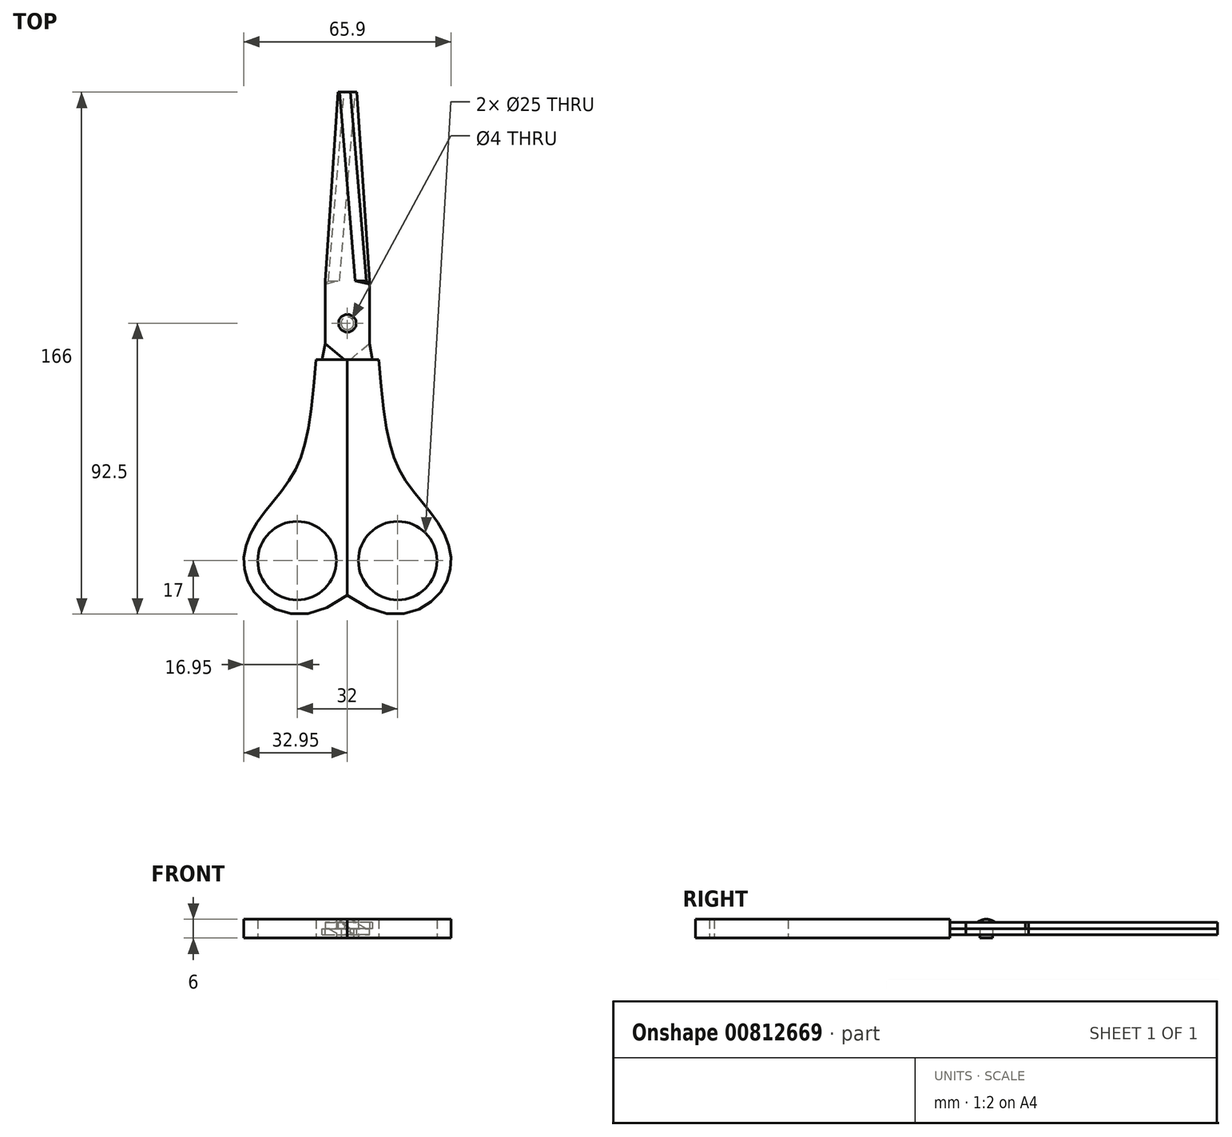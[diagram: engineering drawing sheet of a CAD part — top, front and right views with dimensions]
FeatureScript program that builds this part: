
annotation { "Feature Type Name" : "Feature", "Feature Type Description" : "" }
export const myFeature = defineFeature(function(context is Context, id is Id, definition is map)
    precondition{}
    {
        {
            var Q0;
            Q0=qCreatedBy(makeId("Top.planeOp"),FACE);
            var sketch = newSketch(context, id + "F0", { "sketchPlane" : qUnion([Q0])});
            skLineSegment(sketch, "E0", {"start": v(10, 0) * mm, "end": v(0, 0) * mm});
            skLineSegment(sketch, "E1", {"start": v(0, 0) * mm, "end": v(0, -75) * mm});
            skFitSpline(sketch, "E2", {"points": [v(10, 0) * mm, v(18.6, -38.65) * mm, v(31.21, -56.2) * mm, v(29.97, -73.56) * mm, v(0, -75) * mm], "startDerivative": vector(15.7, -213.23) * mm, "endDerivative": vector(-155.18, 117.57) * mm});
            skSolve(sketch);
        }
        {
            var Q0;
            Q0 = qSketchRegion(id + "F0", true);
            extrude(context, id + "F1", {"entities" : qUnion([Q0]), "depth" : 6 * mm, "offsetDistance" : 25 * mm});
        }
        {
            var Q0;
            Q0=qCreatedBy(makeId("Top.planeOp"),FACE);
            var sketch = newSketch(context, id + "F2", { "sketchPlane" : qUnion([Q0])});
            skCircle(sketch, "E3", {"center": v(16, -64) * mm, "radius": 12.5 * mm});
            skSolve(sketch);
        }
        {
            var Q0;
            Q0 = qSketchRegion(id + "F2", true);
            extrude(context, id + "F3", {"entities" : qUnion([Q0]), "depth" : 6 * mm, "offsetDistance" : 25 * mm});
        }
        {
            var Q0;
            Q0=makeQuery(id+"F3.opExtrude","SWEPT_BODY",BODY,{"disambiguationData":[OSD([sQuery(id+"F2.wireOp",EDGE,"E3")])]});
            var Q1;
            Q1=makeQuery(id+"F1.opExtrude","SWEPT_BODY",BODY,{"disambiguationData":[OSD([sQuery(id+"F0.wireOp",EDGE,"E0"),sQuery(id+"F0.wireOp",EDGE,"E1"),sQuery(id+"F0.wireOp",EDGE,"E2")])]});
            booleanBodies(context, id + "F4", {"operationType" : BooleanOperationType.SUBTRACTION, "tools" : qUnion([Q0]), "targets" : qUnion([Q1])});
        }
        {
            var Q0;
            Q0=makeQuery(id+"F1.opExtrude","SWEPT_BODY",BODY,{"disambiguationData":[OSD([sQuery(id+"F0.wireOp",EDGE,"E0"),sQuery(id+"F0.wireOp",EDGE,"E1"),sQuery(id+"F0.wireOp",EDGE,"E2")])]});
            var Q1;
            Q1=qCreatedBy(makeId("Right.planeOp"),FACE);
            mirror(context, id + "F5", {"entities" : qUnion([Q0]), "mirrorPlane" : qUnion([Q1])});
        }
        {
            var Q0;
            Q0=qCreatedBy(makeId("Top.planeOp"),FACE);
            var Q1;
            Q1 = qBodyType(qCreatedBy(id + "F12" ,EDGE), BodyType.WIRE);
            cPlane(context, id + "F6", {"entities" : qUnion([Q0, Q1]), "cplaneType" : CPlaneType.OFFSET, "offset" : 3 * mm, "width" : 150 * mm, "height" : 150 * mm});
        }
        {
            var Q0;
            Q0=qCreatedBy(makeId("Front.planeOp"),FACE);
            var Q1;
            Q1 = qBodyType(qCreatedBy(id + "F12" ,EDGE), BodyType.WIRE);
            cPlane(context, id + "F7", {"entities" : qUnion([Q0, Q1]), "cplaneType" : CPlaneType.OFFSET, "offset" : 5 * mm, "oppositeDirection" : true, "width" : 150 * mm, "height" : 150 * mm});
        }
        {
            var Q0;
            Q0=qCreatedBy(makeId("Front.planeOp"),FACE);
            cPlane(context, id + "F8", {"entities" : qUnion([Q0]), "cplaneType" : CPlaneType.OFFSET, "offset" : 15 * mm, "oppositeDirection" : true, "width" : 150 * mm, "height" : 150 * mm});
        }
        {
            var Q0;
            Q0=qCreatedBy(makeId("Front.planeOp"),FACE);
            cPlane(context, id + "F9", {"entities" : qUnion([Q0]), "cplaneType" : CPlaneType.OFFSET, "offset" : 25 * mm, "oppositeDirection" : true, "width" : 150 * mm, "height" : 150 * mm});
        }
        {
            var Q0;
            Q0=qCreatedBy(makeId("Front.planeOp"),FACE);
            cPlane(context, id + "F10", {"entities" : qUnion([Q0]), "cplaneType" : CPlaneType.OFFSET, "offset" : 85 * mm, "oppositeDirection" : true, "width" : 150 * mm, "height" : 150 * mm});
        }
        {
            var Q0;
            Q0=qCreatedBy(makeId("Front.planeOp"),FACE);
            cPlane(context, id + "F11", {"entities" : qUnion([Q0]), "cplaneType" : CPlaneType.OFFSET, "offset" : 24 * mm, "oppositeDirection" : true, "width" : 150 * mm, "height" : 150 * mm});
        }
        {
            var Q0;
            Q0=qCreatedBy(makeId("Front.planeOp"),FACE);
            var sketch = newSketch(context, id + "F12", { "sketchPlane" : qUnion([Q0])});
            skLineSegment(sketch, "E4.bottom", {"start": v(8, 5) * mm, "end": v(-1, 5) * mm});
            skLineSegment(sketch, "E4.top", {"start": v(8, 3) * mm, "end": v(-1, 3) * mm});
            skLineSegment(sketch, "E4.left", {"start": v(8, 5) * mm, "end": v(8, 3) * mm});
            skLineSegment(sketch, "E4.right", {"start": v(-1, 5) * mm, "end": v(-1, 3) * mm});
            skSolve(sketch);
        }
        {
            var Q0;
            Q0=qCreatedBy(id+"F7.planeOp",FACE);
            var sketch = newSketch(context, id + "F13", { "sketchPlane" : qUnion([Q0])});
            skLineSegment(sketch, "E5.bottom", {"start": v(7, 5) * mm, "end": v(-7, 5) * mm});
            skLineSegment(sketch, "E5.top", {"start": v(7, 3) * mm, "end": v(-7, 3) * mm});
            skLineSegment(sketch, "E5.left", {"start": v(7, 5) * mm, "end": v(7, 3) * mm});
            skLineSegment(sketch, "E5.right", {"start": v(-7, 5) * mm, "end": v(-7, 3) * mm});
            skSolve(sketch);
        }
        {
            var Q0;
            Q0=qCreatedBy(id+"F10.planeOp",FACE);
            var sketch = newSketch(context, id + "F14", { "sketchPlane" : qUnion([Q0])});
            skLineSegment(sketch, "E6", {"start": v(-2.5, 5) * mm, "end": v(-3, 5) * mm});
            skLineSegment(sketch, "E7", {"start": v(-3, 5) * mm, "end": v(-3, 3) * mm});
            skLineSegment(sketch, "E8", {"start": v(-3, 3) * mm, "end": v(1, 3) * mm});
            skLineSegment(sketch, "E9", {"start": v(1, 3) * mm, "end": v(-2.5, 5) * mm});
            skSolve(sketch);
        }
        {
            var Q0;
            Q0=qCreatedBy(id+"F8.planeOp",FACE);
            var sketch = newSketch(context, id + "F15", { "sketchPlane" : qUnion([Q0])});
            skLineSegment(sketch, "E10", {"start": v(-7, 5) * mm, "end": v(6, 5) * mm});
            skLineSegment(sketch, "E11", {"start": v(6, 5) * mm, "end": v(6, 3) * mm});
            skLineSegment(sketch, "E12", {"start": v(6, 3) * mm, "end": v(-7, 3) * mm});
            skLineSegment(sketch, "E13", {"start": v(-7, 3) * mm, "end": v(-7, 5) * mm});
            skSolve(sketch);
        }
        {
            var Q0;
            Q0=qCreatedBy(id+"F9.planeOp",FACE);
            var sketch = newSketch(context, id + "F16", { "sketchPlane" : qUnion([Q0])});
            skLineSegment(sketch, "E14", {"start": v(-7, 3) * mm, "end": v(6, 3) * mm});
            skLineSegment(sketch, "E15", {"start": v(6, 3) * mm, "end": v(2.5, 5) * mm});
            skLineSegment(sketch, "E16", {"start": v(2.5, 5) * mm, "end": v(-7, 5) * mm});
            skLineSegment(sketch, "E17", {"start": v(-7, 5) * mm, "end": v(-7, 3) * mm});
            skSolve(sketch);
        }
        {
            var Q0;
            Q0=qCreatedBy(id+"F11.planeOp",FACE);
            var sketch = newSketch(context, id + "F17", { "sketchPlane" : qUnion([Q0])});
            skLineSegment(sketch, "E18", {"start": v(-7, 5) * mm, "end": v(7, 5) * mm});
            skLineSegment(sketch, "E19", {"start": v(7, 5) * mm, "end": v(7, 3) * mm});
            skLineSegment(sketch, "E20", {"start": v(7, 3) * mm, "end": v(-7, 3) * mm});
            skLineSegment(sketch, "E21", {"start": v(-7, 3) * mm, "end": v(-7, 5) * mm});
            skSolve(sketch);
        }
        {
            var Q1;
            Q1=makeQuery(id+"F12.imprint","IMPRINT",FACE,{"disambiguationData":[TD([[makeQuery(id+"F12.imprint","IMPRINT",EDGE,{"derivedFrom":sQuery(id+"F12.wireOp",EDGE,"E4.bottom")}),1.0]])]});
            var Q2;
            Q2=makeQuery(id+"F13.imprint","IMPRINT",FACE,{"disambiguationData":[TD([[makeQuery(id+"F13.imprint","IMPRINT",EDGE,{"derivedFrom":sQuery(id+"F13.wireOp",EDGE,"E5.bottom")}),1.0]])]});
            loft(context, id + "F18", {"sheetProfilesArray" : [{ "sheetProfileEntities" : qUnion([Q1]) }, { "sheetProfileEntities" : qUnion([Q2]) }]});
        }
        {
            var Q0;
            Q0=qCreatedBy(id+"F6.planeOp",FACE);
            var sketch = newSketch(context, id + "F19", { "sketchPlane" : qUnion([Q0])});
            skLineSegment(sketch, "E22", {"start": v(0, 0) * mm, "end": v(0, 90) * mm});
            skSolve(sketch);
        }
        {
            var Q1;
            Q1=makeQuery(id+"F13.imprint","IMPRINT",FACE,{"disambiguationData":[TD([[makeQuery(id+"F13.imprint","IMPRINT",EDGE,{"derivedFrom":sQuery(id+"F13.wireOp",EDGE,"E5.bottom")}),1.0]])]});
            var Q2;
            Q2=makeQuery(id+"F17.imprint","IMPRINT",FACE,{"disambiguationData":[TD([[makeQuery(id+"F17.imprint","IMPRINT",EDGE,{"derivedFrom":sQuery(id+"F17.wireOp",EDGE,"E18")}),-1.0]])]});
            loft(context, id + "F20", {"operationType" : NewBodyOperationType.ADD, "sheetProfilesArray" : [{ "sheetProfileEntities" : qUnion([Q1]) }, { "sheetProfileEntities" : qUnion([Q2]) }]});
        }
        {
            var Q1;
            Q1=makeQuery(id+"F20.opLoft","CAP_FACE",FACE,{"disambiguationData":[OSD([makeQuery(id+"F17.imprint","IMPRINT",FACE,{"disambiguationData":[TD([[makeQuery(id+"F17.imprint","IMPRINT",EDGE,{"derivedFrom":sQuery(id+"F17.wireOp",EDGE,"E18")}),-1.0]])]})])],"isStart":true});
            var Q2;
            Q2=makeQuery(id+"F16.imprint","IMPRINT",FACE,{"disambiguationData":[TD([[makeQuery(id+"F16.imprint","IMPRINT",EDGE,{"derivedFrom":sQuery(id+"F16.wireOp",EDGE,"E14")}),1.0]])]});
            loft(context, id + "F21", {"operationType" : NewBodyOperationType.ADD, "sheetProfilesArray" : [{ "sheetProfileEntities" : qUnion([Q1]) }, { "sheetProfileEntities" : qUnion([Q2]) }]});
        }
        {
            var Q1;
            Q1=makeQuery(id+"F21.opLoft","CAP_FACE",FACE,{"disambiguationData":[OSD([makeQuery(id+"F16.imprint","IMPRINT",FACE,{"disambiguationData":[TD([[makeQuery(id+"F16.imprint","IMPRINT",EDGE,{"derivedFrom":sQuery(id+"F16.wireOp",EDGE,"E14")}),1.0]])]})])],"isStart":true});
            var Q2;
            Q2=makeQuery(id+"F14.imprint","IMPRINT",FACE,{"disambiguationData":[TD([[makeQuery(id+"F14.imprint","IMPRINT",EDGE,{"derivedFrom":sQuery(id+"F14.wireOp",EDGE,"E6")}),1.0]])]});
            loft(context, id + "F22", {"operationType" : NewBodyOperationType.ADD, "sheetProfilesArray" : [{ "sheetProfileEntities" : qUnion([Q1]) }, { "sheetProfileEntities" : qUnion([Q2]) }]});
        }
        {
            var Q0;
            Q0=makeQuery(id+"F18.opLoft","SWEPT_BODY",BODY,{"disambiguationData":[OSD([makeQuery(id+"F12.imprint","IMPRINT",FACE,{"disambiguationData":[TD([[makeQuery(id+"F12.imprint","IMPRINT",EDGE,{"derivedFrom":sQuery(id+"F12.wireOp",EDGE,"E4.bottom")}),1.0]])]}),makeQuery(id+"F13.imprint","IMPRINT",FACE,{"disambiguationData":[TD([[makeQuery(id+"F13.imprint","IMPRINT",EDGE,{"derivedFrom":sQuery(id+"F13.wireOp",EDGE,"E5.bottom")}),1.0]])]})])]});
            var Q1;
            Q1=sQuery(id+"F19.wireOp",EDGE,"E22");
            transform(context, id + "F23", {"entities" : qUnion([Q0]), "transformType" : TransformType.ROTATION, "transformAxis" : qUnion([Q1]), "angle" : 180 * degree, "makeCopy" : true});
        }
        {
            var Q0;
            Q0=qCreatedBy(makeId("Top.planeOp"),FACE);
            var sketch = newSketch(context, id + "F24", { "sketchPlane" : qUnion([Q0])});
            skCircle(sketch, "E23", {"center": v(0, 11.5) * mm, "radius": 2 * mm});
            skSolve(sketch);
        }
        {
            var Q0;
            Q0 = qSketchRegion(id + "F24", true);
            extrude(context, id + "F25", {"entities" : qUnion([Q0]), "depth" : 5.5 * mm, "offsetDistance" : 25 * mm});
        }
        {
            var Q0;
            Q0=makeQuery(id+"F25.opExtrude","SWEPT_BODY",BODY,{"disambiguationData":[OSD([sQuery(id+"F24.wireOp",EDGE,"E23")])]});
            var Q1;
            Q1=makeQuery(id+"F18.opLoft","SWEPT_BODY",BODY,{"disambiguationData":[OSD([makeQuery(id+"F12.imprint","IMPRINT",FACE,{"disambiguationData":[TD([[makeQuery(id+"F12.imprint","IMPRINT",EDGE,{"derivedFrom":sQuery(id+"F12.wireOp",EDGE,"E4.bottom")}),1.0]])]}),makeQuery(id+"F13.imprint","IMPRINT",FACE,{"disambiguationData":[TD([[makeQuery(id+"F13.imprint","IMPRINT",EDGE,{"derivedFrom":sQuery(id+"F13.wireOp",EDGE,"E5.bottom")}),1.0]])]})])]});
            var Q2;
            Q2=makeQuery(id+"F23.opPattern","COPY",BODY,{"derivedFrom":makeQuery(id+"F18.opLoft","SWEPT_BODY",BODY,{"disambiguationData":[OSD([makeQuery(id+"F12.imprint","IMPRINT",FACE,{"disambiguationData":[TD([[makeQuery(id+"F12.imprint","IMPRINT",EDGE,{"derivedFrom":sQuery(id+"F12.wireOp",EDGE,"E4.bottom")}),1.0]])]}),makeQuery(id+"F13.imprint","IMPRINT",FACE,{"disambiguationData":[TD([[makeQuery(id+"F13.imprint","IMPRINT",EDGE,{"derivedFrom":sQuery(id+"F13.wireOp",EDGE,"E5.bottom")}),1.0]])]})])]}),"instanceName":"1"});
            booleanBodies(context, id + "F26", {"operationType" : BooleanOperationType.SUBTRACTION, "tools" : qUnion([Q0]), "targets" : qUnion([Q1, Q2]), "keepTools" : true});
        }
        {
            var Q0;
            Q0=qCreatedBy(makeId("Front.planeOp"),FACE);
            cPlane(context, id + "F27", {"entities" : qUnion([Q0]), "cplaneType" : CPlaneType.OFFSET, "offset" : 11.5 * mm, "oppositeDirection" : true, "width" : 150 * mm, "height" : 150 * mm});
        }
        {
            var Q0;
            Q0=qCreatedBy(id+"F27.planeOp",FACE);
            var sketch = newSketch(context, id + "F28", { "sketchPlane" : qUnion([Q0])});
            skArc(sketch, "E24", {"start": v(2.8, 5) * mm, "mid": v(1.49, 5.74) * mm, "end": v(0, 6) * mm});
            skLineSegment(sketch, "E25", {"start": v(2.8, 5) * mm, "end": v(0, 5) * mm});
            skLineSegment(sketch, "E26", {"start": v(0, 5) * mm, "end": v(0, 6) * mm});
            skSolve(sketch);
        }
        {
            var Q0;
            Q0=makeQuery(id+"F28.imprint","IMPRINT",FACE,{"disambiguationData":[TD([[makeQuery(id+"F28.imprint","IMPRINT",EDGE,{"derivedFrom":sQuery(id+"F28.wireOp",EDGE,"E24")}),1.0]])]});
            var Q1;
            Q1=sQuery(id+"F28.wireOp",EDGE,"E26");
            revolve(context, id + "F29", {"operationType" : NewBodyOperationType.ADD, "surfaceOperationType" : NewSurfaceOperationType.NEW, "entities" : qUnion([Q0]), "axis" : qUnion([Q1]), "revolveType" : RevolveType.FULL});
        }
    });
